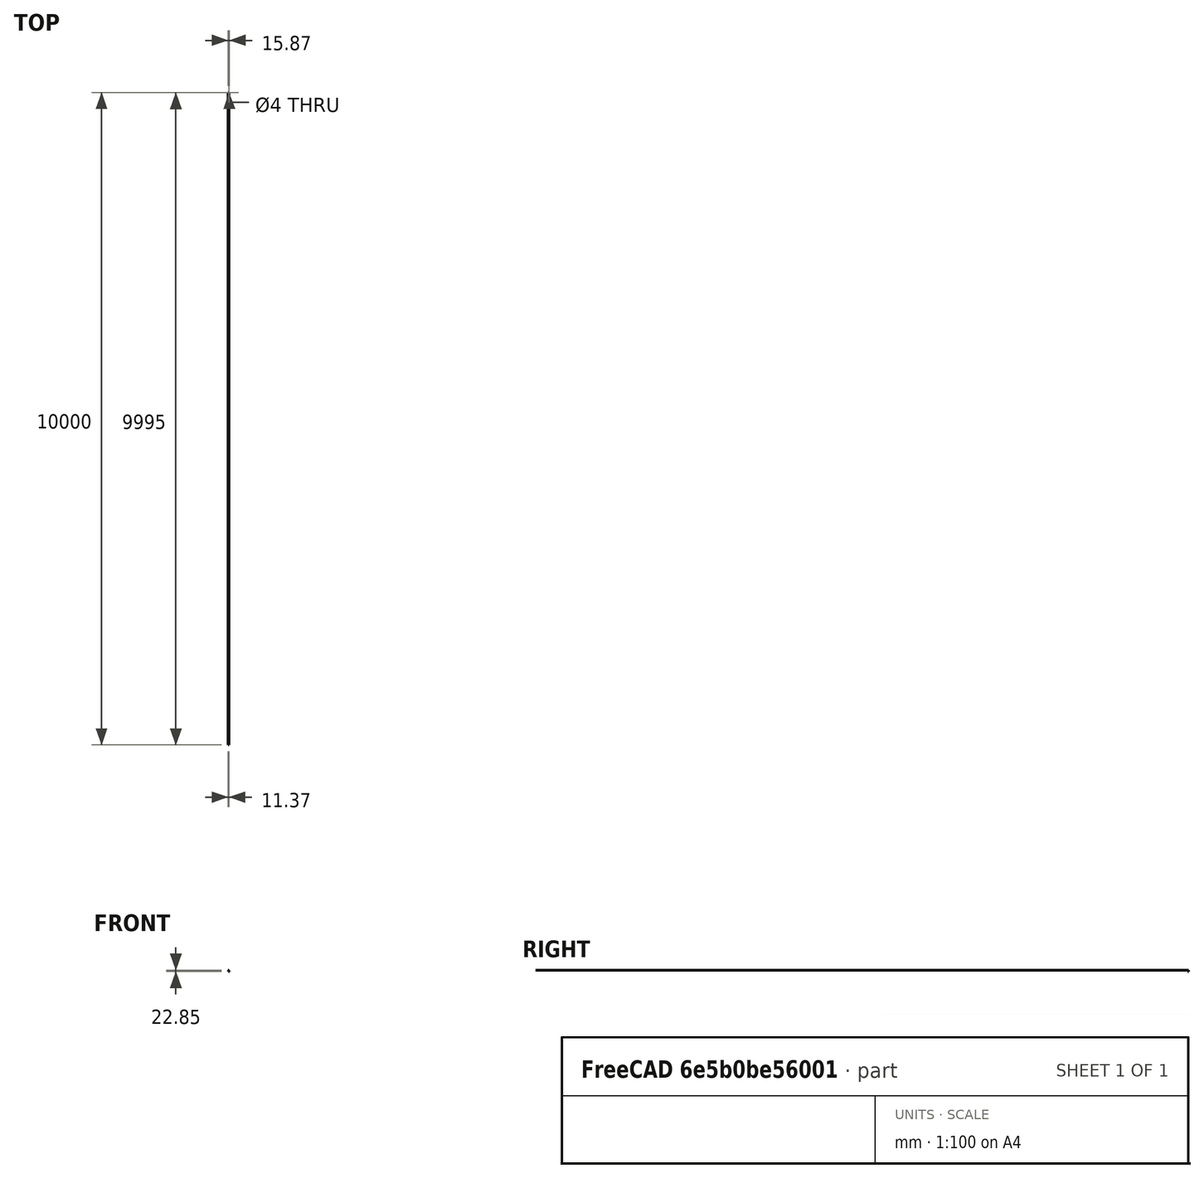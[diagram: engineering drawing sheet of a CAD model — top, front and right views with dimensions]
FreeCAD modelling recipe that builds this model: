
FCSTD DOCUMENT  (FreeCAD 0.15R4671 (Git))
Label: gluty feed guide
License: All rights reserved
LicenseURL: http://en.wikipedia.org/wiki/All_rights_reserved
objects: Part::Feature×1, Sketcher::SketchObject×1, PartDesign::Pocket×1
note: 4 computed .brp shape members not serialized (recipe doc carries the construction recipe); baked Part::Feature solids carry a one-line shape summary decoded from their .brp

FEATURE [Part::Feature] Part__Feature  label="Pocket003"
  shape: bbox 13.5 x 10 x 20.5 mm, 13 faces (baked)
FEATURE [Sketcher::SketchObject] Sketch
  Placement = pos=(0,0,0) rot=(0,0.707107,0.707107;3.14159rad)
  Support = -> Part__Feature [Face3]
  sketch-geometry (3):
    g0: LineSegment StartX=-6.51545 StartY=20.547 StartZ=0 EndX=2.36766 EndY=18.7394 EndZ=0
    g1: LineSegment StartX=2.36766 StartY=18.7394 StartZ=0 EndX=2.36766 EndY=22.8456 EndZ=0
    g2: LineSegment StartX=2.36766 StartY=22.8456 StartZ=0 EndX=-6.51545 EndY=20.547 EndZ=0
  constraints (4):
    c: Coincident(g0,g1)
    c: Vertical(g1)
    c: Coincident(g1,g2)
    c: Coincident(g2,g0)
FEATURE [PartDesign::Pocket] Pocket
  Length = 5
  Sketch = -> Sketch
  Type = 1
